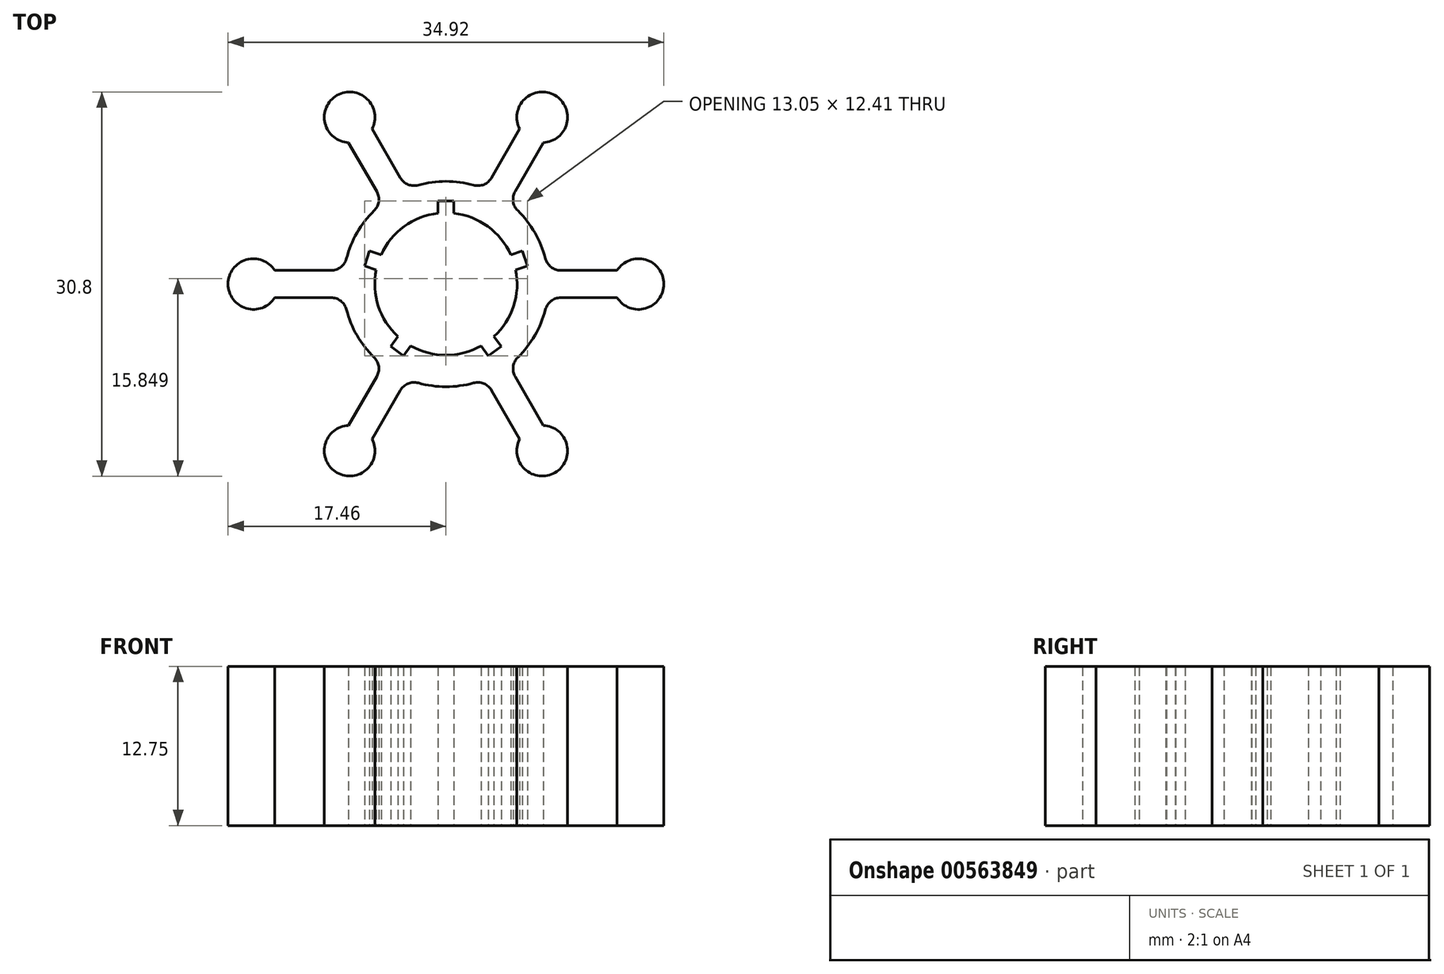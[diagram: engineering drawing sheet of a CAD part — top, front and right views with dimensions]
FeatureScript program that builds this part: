
annotation { "Feature Type Name" : "Feature", "Feature Type Description" : "" }
export const myFeature = defineFeature(function(context is Context, id is Id, definition is map)
    precondition{}
    {
        {
            var Q0;
            Q0=qCreatedBy(makeId("Top.planeOp"),FACE);
            var sketch = newSketch(context, id + "F0", { "sketchPlane" : qUnion([Q0])});
            skArc(sketch, "E0", {"start": v(-0.64, 5.67) * mm, "mid": v(-3.35, 4.61) * mm, "end": v(-5.2, 2.36) * mm});
            skArc(sketch, "E1", {"start": v(-3.13, -7.61) * mm, "mid": v(0, -8.23) * mm, "end": v(3.13, -7.61) * mm});
            skArc(sketch, "E2", {"start": v(2.4, -3.15) * mm, "mid": v(0, 3.96) * mm, "end": v(-2.4, -3.15) * mm});
            skLineSegment(sketch, "E3.trimOffspring", {"start": v(2.4, -3.15) * mm, "end": v(-2.4, -3.15) * mm});
            skLineSegment(sketch, "E4", {"start": v(8.23, 0) * mm, "end": v(19.44, 0) * mm});
            skLineSegment(sketch, "E5.3.0", {"start": v(-8.16, -1.1) * mm, "end": v(-13.72, -1.1) * mm});
            skLineSegment(sketch, "E5.3.1", {"start": v(-8.16, 1.1) * mm, "end": v(-13.72, 1.1) * mm});
            skPoint(sketch, "E6.orphan", {"position": v(-8.23, 1.1) * mm});
            skPoint(sketch, "E7.orphan", {"position": v(-8.23, -1.1) * mm});
            skPoint(sketch, "E8.orphan", {"position": v(-5.06, -6.58) * mm});
            skPoint(sketch, "E9.orphan", {"position": v(-3.17, -7.67) * mm});
            skPoint(sketch, "E10.orphan", {"position": v(3.17, -7.67) * mm});
            skPoint(sketch, "E11.orphan", {"position": v(5.06, -6.58) * mm});
            skPoint(sketch, "E12.orphan", {"position": v(8.23, -1.1) * mm});
            skPoint(sketch, "E13.orphan", {"position": v(8.23, 1.1) * mm});
            skPoint(sketch, "E14.orphan", {"position": v(5.06, 6.58) * mm});
            skPoint(sketch, "E15.orphan", {"position": v(3.17, 7.67) * mm});
            skPoint(sketch, "E16.orphan", {"position": v(-3.17, 7.67) * mm});
            skPoint(sketch, "E17.orphan", {"position": v(-5.06, 6.58) * mm});
            skArc(sketch, "E18.trimOffspring", {"start": v(5.02, -6.52) * mm, "mid": v(7.13, -4.11) * mm, "end": v(8.16, -1.1) * mm});
            skArc(sketch, "E19.trimOffspring", {"start": v(8.16, 1.1) * mm, "mid": v(7.13, 4.11) * mm, "end": v(5.02, 6.52) * mm});
            skArc(sketch, "E20.trimOffspring", {"start": v(3.13, 7.61) * mm, "mid": v(0, 8.23) * mm, "end": v(-3.13, 7.61) * mm});
            skArc(sketch, "E21.trimOffspring", {"start": v(-5.02, 6.52) * mm, "mid": v(-7.13, 4.11) * mm, "end": v(-8.16, 1.1) * mm});
            skArc(sketch, "E22.trimOffspring", {"start": v(-8.16, -1.1) * mm, "mid": v(-7.13, -4.11) * mm, "end": v(-5.02, -6.52) * mm});
            skArc(sketch, "E23", {"start": v(-13.72, 1.1) * mm, "mid": v(-17.46, 0) * mm, "end": v(-13.72, -1.1) * mm});
            skArc(sketch, "E24.1.0", {"start": v(-7.8, -11.33) * mm, "mid": v(-8.73, -15.12) * mm, "end": v(-5.91, -12.43) * mm});
            skLineSegment(sketch, "E24.1.1", {"start": v(-3.13, -7.61) * mm, "end": v(-5.91, -12.43) * mm});
            skLineSegment(sketch, "E24.1.2", {"start": v(-5.02, -6.52) * mm, "end": v(-7.8, -11.33) * mm});
            skArc(sketch, "E24.2.0", {"start": v(5.91, -12.43) * mm, "mid": v(8.73, -15.12) * mm, "end": v(7.8, -11.33) * mm});
            skLineSegment(sketch, "E24.2.1", {"start": v(5.02, -6.52) * mm, "end": v(7.8, -11.33) * mm});
            skLineSegment(sketch, "E24.2.2", {"start": v(3.13, -7.61) * mm, "end": v(5.91, -12.43) * mm});
            skArc(sketch, "E24.3.0", {"start": v(13.72, -1.1) * mm, "mid": v(17.46, 0) * mm, "end": v(13.72, 1.1) * mm});
            skLineSegment(sketch, "E24.3.1", {"start": v(8.16, 1.1) * mm, "end": v(13.72, 1.1) * mm});
            skLineSegment(sketch, "E24.3.2", {"start": v(8.16, -1.1) * mm, "end": v(13.72, -1.1) * mm});
            skArc(sketch, "E24.4.0", {"start": v(7.8, 11.33) * mm, "mid": v(8.73, 15.12) * mm, "end": v(5.91, 12.43) * mm});
            skLineSegment(sketch, "E24.4.1", {"start": v(3.13, 7.61) * mm, "end": v(5.91, 12.43) * mm});
            skLineSegment(sketch, "E24.4.2", {"start": v(5.02, 6.52) * mm, "end": v(7.8, 11.33) * mm});
            skArc(sketch, "E24.5.0", {"start": v(-5.91, 12.43) * mm, "mid": v(-8.73, 15.12) * mm, "end": v(-7.8, 11.33) * mm});
            skLineSegment(sketch, "E24.5.1", {"start": v(-5.02, 6.52) * mm, "end": v(-7.8, 11.33) * mm});
            skLineSegment(sketch, "E24.5.2", {"start": v(-3.13, 7.61) * mm, "end": v(-5.91, 12.43) * mm});
            skLineSegment(sketch, "E25.top", {"start": v(0.63, 6.65) * mm, "end": v(-0.64, 6.65) * mm});
            skLineSegment(sketch, "E25.left", {"start": v(0.63, 5.67) * mm, "end": v(0.63, 6.65) * mm});
            skLineSegment(sketch, "E25.right", {"start": v(-0.64, 5.67) * mm, "end": v(-0.64, 6.65) * mm});
            skPoint(sketch, "E25.middle", {"position": v(0, 5.7) * mm});
            skPoint(sketch, "E26.orphan", {"position": v(0.63, 4.75) * mm});
            skPoint(sketch, "E27.orphan", {"position": v(-0.64, 4.75) * mm});
            skLineSegment(sketch, "E28.1.0", {"start": v(-6.13, 2.66) * mm, "end": v(-6.53, 1.45) * mm});
            skLineSegment(sketch, "E28.1.1", {"start": v(-5.2, 2.36) * mm, "end": v(-6.13, 2.66) * mm});
            skLineSegment(sketch, "E28.1.2", {"start": v(-5.59, 1.15) * mm, "end": v(-6.53, 1.45) * mm});
            skLineSegment(sketch, "E28.2.0", {"start": v(-4.43, -5.01) * mm, "end": v(-3.4, -5.76) * mm});
            skLineSegment(sketch, "E28.2.1", {"start": v(-3.84, -4.21) * mm, "end": v(-4.43, -5.01) * mm});
            skLineSegment(sketch, "E28.2.2", {"start": v(-2.82, -4.96) * mm, "end": v(-3.4, -5.76) * mm});
            skLineSegment(sketch, "E28.3.0", {"start": v(3.4, -5.76) * mm, "end": v(4.43, -5.01) * mm});
            skLineSegment(sketch, "E28.3.1", {"start": v(2.82, -4.96) * mm, "end": v(3.4, -5.76) * mm});
            skLineSegment(sketch, "E28.3.2", {"start": v(3.84, -4.21) * mm, "end": v(4.43, -5.01) * mm});
            skLineSegment(sketch, "E28.4.0", {"start": v(6.53, 1.45) * mm, "end": v(6.13, 2.66) * mm});
            skLineSegment(sketch, "E28.4.1", {"start": v(5.59, 1.15) * mm, "end": v(6.53, 1.45) * mm});
            skLineSegment(sketch, "E28.4.2", {"start": v(5.2, 2.36) * mm, "end": v(6.13, 2.66) * mm});
            skArc(sketch, "E29.trimOffspring", {"start": v(-5.59, 1.15) * mm, "mid": v(-5.42, -1.76) * mm, "end": v(-3.84, -4.21) * mm});
            skArc(sketch, "E30.trimOffspring", {"start": v(5.2, 2.36) * mm, "mid": v(3.35, 4.61) * mm, "end": v(0.63, 5.67) * mm});
            skArc(sketch, "E31.trimOffspring", {"start": v(-2.82, -4.96) * mm, "mid": v(0, -5.7) * mm, "end": v(2.82, -4.96) * mm});
            skArc(sketch, "E32.trimOffspring", {"start": v(3.84, -4.21) * mm, "mid": v(5.42, -1.76) * mm, "end": v(5.59, 1.15) * mm});
            skSolve(sketch);
        }
        {
            var Q0;
            Q0=makeQuery(id+"F0.imprint","IMPRINT",FACE,{"disambiguationData":[TD([[makeQuery(id+"F0.imprint","IMPRINT",EDGE,{"derivedFrom":sQuery(id+"F0.wireOp",EDGE,"E0")}),-1.0]])]});
            extrude(context, id + "F1", {"entities" : qUnion([Q0]), "depth" : 12.75 * mm, "offsetDistance" : 25.4 * mm});
        }
        {
            var Q0;
            Q0=makeQuery(id+"F1.opExtrude","SWEPT_EDGE",EDGE,{"disambiguationData":[OSD([sQuery(id+"F0.wireOp",EDGE,"E20.trimOffspring"),sQuery(id+"F0.wireOp",EDGE,"E24.5.2")])]});
            var Q1;
            Q1=makeQuery(id+"F1.opExtrude","SWEPT_EDGE",EDGE,{"disambiguationData":[OSD([sQuery(id+"F0.wireOp",EDGE,"E19.trimOffspring"),sQuery(id+"F0.wireOp",EDGE,"E24.4.2")])]});
            var Q2;
            Q2=makeQuery(id+"F1.opExtrude","SWEPT_EDGE",EDGE,{"disambiguationData":[OSD([sQuery(id+"F0.wireOp",EDGE,"E19.trimOffspring"),sQuery(id+"F0.wireOp",EDGE,"E24.3.1")])]});
            var Q3;
            Q3=makeQuery(id+"F1.opExtrude","SWEPT_EDGE",EDGE,{"disambiguationData":[OSD([sQuery(id+"F0.wireOp",EDGE,"E20.trimOffspring"),sQuery(id+"F0.wireOp",EDGE,"E24.4.1")])]});
            var Q4;
            Q4=makeQuery(id+"F1.opExtrude","SWEPT_EDGE",EDGE,{"disambiguationData":[OSD([sQuery(id+"F0.wireOp",EDGE,"E21.trimOffspring"),sQuery(id+"F0.wireOp",EDGE,"E24.5.1")])]});
            var Q5;
            Q5=makeQuery(id+"F1.opExtrude","SWEPT_EDGE",EDGE,{"disambiguationData":[OSD([sQuery(id+"F0.wireOp",EDGE,"E5.3.1"),sQuery(id+"F0.wireOp",EDGE,"E21.trimOffspring")])]});
            var Q6;
            Q6=makeQuery(id+"F1.opExtrude","SWEPT_EDGE",EDGE,{"disambiguationData":[OSD([sQuery(id+"F0.wireOp",EDGE,"E22.trimOffspring"),sQuery(id+"F0.wireOp",EDGE,"E24.1.2")])]});
            var Q7;
            Q7=makeQuery(id+"F1.opExtrude","SWEPT_EDGE",EDGE,{"disambiguationData":[OSD([sQuery(id+"F0.wireOp",EDGE,"E5.3.0"),sQuery(id+"F0.wireOp",EDGE,"E22.trimOffspring")])]});
            var Q8;
            Q8=makeQuery(id+"F1.opExtrude","SWEPT_EDGE",EDGE,{"disambiguationData":[OSD([sQuery(id+"F0.wireOp",EDGE,"E1"),sQuery(id+"F0.wireOp",EDGE,"E24.1.1")])]});
            var Q9;
            Q9=makeQuery(id+"F1.opExtrude","SWEPT_EDGE",EDGE,{"disambiguationData":[OSD([sQuery(id+"F0.wireOp",EDGE,"E1"),sQuery(id+"F0.wireOp",EDGE,"E24.2.2")])]});
            var Q10;
            Q10=makeQuery(id+"F1.opExtrude","SWEPT_EDGE",EDGE,{"disambiguationData":[OSD([sQuery(id+"F0.wireOp",EDGE,"E18.trimOffspring"),sQuery(id+"F0.wireOp",EDGE,"E24.2.1")])]});
            var Q11;
            Q11=makeQuery(id+"F1.opExtrude","SWEPT_EDGE",EDGE,{"disambiguationData":[OSD([sQuery(id+"F0.wireOp",EDGE,"E18.trimOffspring"),sQuery(id+"F0.wireOp",EDGE,"E24.3.2")])]});
            fillet(context, id + "F2", {"entities" : qUnion([Q0, Q1, Q2, Q3, Q4, Q5, Q6, Q7, Q8, Q9, Q10, Q11]), "radius" : 1.27 * mm, "tangentPropagation" : true, "allowEdgeOverflow" : false});
        }
    });
